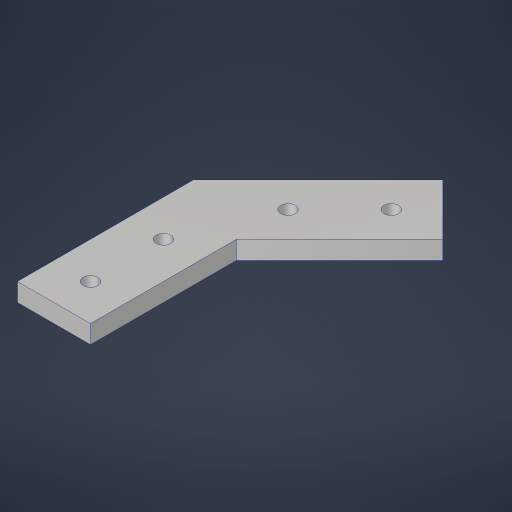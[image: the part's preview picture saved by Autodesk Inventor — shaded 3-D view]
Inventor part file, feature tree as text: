
AUTODESK INVENTOR PART (.ipt)
format: ipt  version: 2023.4 (Build 274418000, 418)  size: 183,296 bytes
history: native  units: in
note: dims shown in document units (in); Inventor stores cm internally (conversion verified against a paired STEP export)
features: sketch x2, extrude x1, hole x1, projected_geometry x1
ambient origin geometry x8: Origin, YZ Plane, XZ Plane, XY Plane, X Axis, Y Axis, Z Axis, Center Point
bodies: Solid1 (feature_tree)
feature tree (5):
  extrude  "Extrusion1"  Depth=1.0in
  hole  "Hole1"  [1 undecoded]
  sketch  "Sketch1"  dims[d0=1.0in d2=1.0in]
  sketch  "Sketch2"  dims[d4=135.0deg d8=2.0in d9=2.0in d10=0.25in d11=0.0in d12=1.0in d13=0.5in d14=1.0in d15=0.5in d16=0.201in d17=0.38in d18=0.385in d19=0.25in d20=0.5635in d21=1.0in d22=0.8108in]
  projected_geometry  "Project Cut Edges1"
note: 1 required parameter value undecoded (feature->parameter linkage not recoverable at this tier; creation-order binding heuristic only, values carry confidence <= 0.55)
